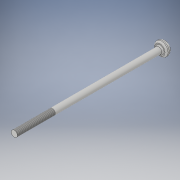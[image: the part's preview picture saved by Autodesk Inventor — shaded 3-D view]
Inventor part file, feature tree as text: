
AUTODESK INVENTOR PART (.ipt)
format: ipt  version: 2019 (Build 230136000, 136)  size: 193,536 bytes
history: native  units: mm
features: fillet x4, sketch x3, extrude x2, thread x1, loft x1
ambient origin geometry x8: Origin, YZ Plane, XZ Plane, XY Plane, X Axis, Y Axis, Z Axis, Center Point
bodies: Solid1 (feature_tree)
feature tree (11):
  sketch  "Sketch1"  dims[d0=0.8mm d1=1.75mm]
  extrude  "Extrusion1"  Depth=1.75mm
  extrude  "Extrusion2"  Depth=0.75mm TaperAngle=0.0deg
  thread  "Thread1"  [1 undecoded]
  fillet  "Fillet1"  Radius=0.4mm
  fillet  "Fillet2"  Radius=0.2mm
  fillet  "Fillet3"  Radius=0.15mm
  loft  "Loft1"
  fillet  "Fillet4"  Radius=0.75mm
  sketch  "Sketch2"  dims[d2=19.0mm d3=0.0mm d4=0.75mm d5=0.0mm d6=5.0mm d7=0.0mm d8=0.4mm d9=0.2mm d10=0.15mm]
  sketch  "Sketch3"  dims[d11=1.5mm d12=0.6mm d13=0.75mm d14=0.0mm d15=90.0deg d16=0.0mm d17=90.0deg d18=0.15mm]
note: 1 required parameter value undecoded (feature->parameter linkage not recoverable at this tier; creation-order binding heuristic only, values carry confidence <= 0.55)
